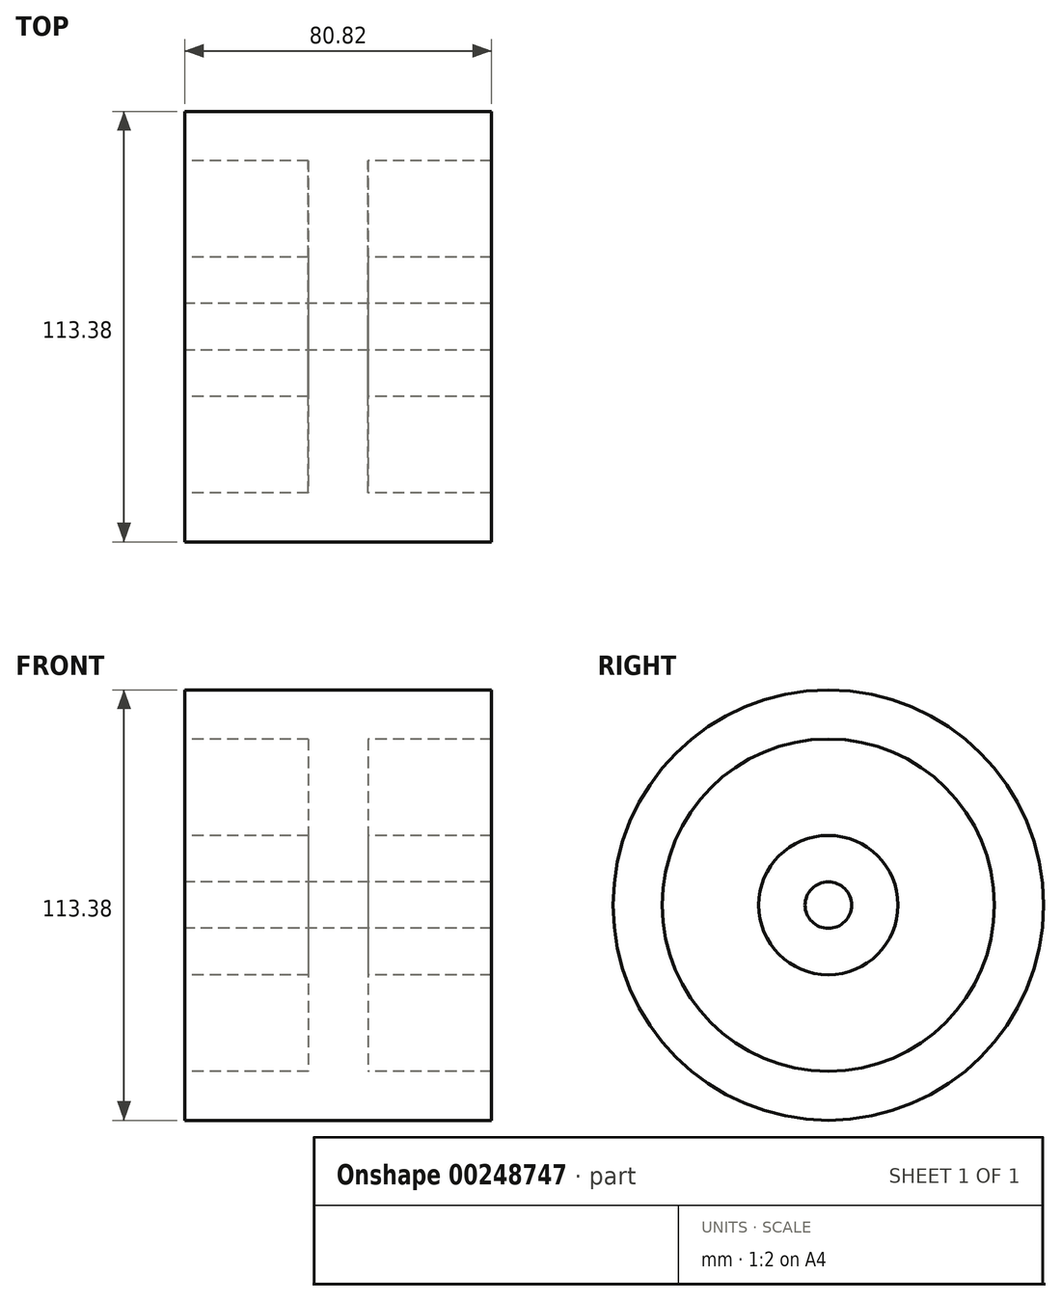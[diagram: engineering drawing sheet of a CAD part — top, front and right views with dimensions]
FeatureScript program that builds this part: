
annotation { "Feature Type Name" : "Feature", "Feature Type Description" : "" }
export const myFeature = defineFeature(function(context is Context, id is Id, definition is map)
    precondition{}
    {
        {
            var Q0;
            Q0=qCreatedBy(makeId("Front.planeOp"),FACE);
            var sketch = newSketch(context, id + "F0", { "sketchPlane" : qUnion([Q0])});
            skLineSegment(sketch, "E0", {"start": v(-76.43, 0) * mm, "end": v(75.74, 0) * mm, "construction": true});
            skLineSegment(sketch, "E1", {"start": v(0, 0) * mm, "end": v(0, 76.32) * mm, "construction": true});
            skLineSegment(sketch, "E2", {"start": v(-40.4, 56.69) * mm, "end": v(40.4, 56.69) * mm});
            skLineSegment(sketch, "E3", {"start": v(-40.4, 56.69) * mm, "end": v(-40.4, 43.76) * mm});
            skLineSegment(sketch, "E4", {"start": v(-40.4, 43.76) * mm, "end": v(-7.85, 43.76) * mm});
            skLineSegment(sketch, "E5", {"start": v(-7.85, 43.76) * mm, "end": v(-7.85, 18.36) * mm});
            skLineSegment(sketch, "E6", {"start": v(-7.85, 18.36) * mm, "end": v(-40.4, 18.36) * mm});
            skLineSegment(sketch, "E7", {"start": v(-40.4, 18.36) * mm, "end": v(-40.4, 6.12) * mm});
            skLineSegment(sketch, "E8", {"start": v(-40.4, 6.12) * mm, "end": v(40.4, 6.12) * mm});
            skLineSegment(sketch, "E9", {"start": v(40.4, 6.12) * mm, "end": v(40.4, 18.36) * mm});
            skLineSegment(sketch, "E10", {"start": v(40.4, 18.36) * mm, "end": v(7.85, 18.36) * mm});
            skLineSegment(sketch, "E11", {"start": v(7.85, 18.36) * mm, "end": v(7.85, 43.76) * mm});
            skLineSegment(sketch, "E12", {"start": v(7.85, 43.76) * mm, "end": v(40.4, 43.76) * mm});
            skLineSegment(sketch, "E13", {"start": v(40.4, 43.76) * mm, "end": v(40.4, 56.69) * mm});
            skSolve(sketch);
        }
        {
            var Q0;
            Q0 = qSketchRegion(id + "F0", true);
            var Q1;
            Q1=sQuery(id+"F0.wireOp",EDGE,"E0");
            revolve(context, id + "F1", {"entities" : qUnion([Q0]), "axis" : qUnion([Q1]), "revolveType" : RevolveType.FULL});
        }
    });
